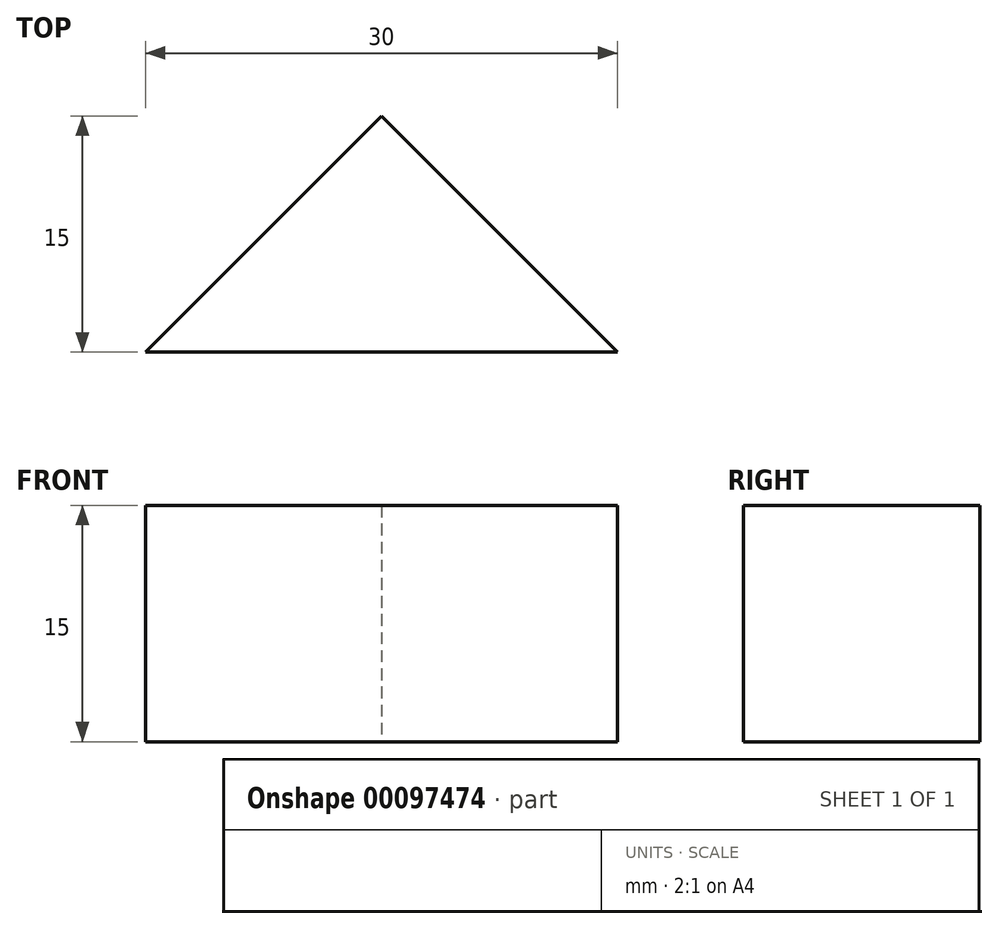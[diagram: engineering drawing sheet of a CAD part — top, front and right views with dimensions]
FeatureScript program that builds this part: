
annotation { "Feature Type Name" : "Feature", "Feature Type Description" : "" }
export const myFeature = defineFeature(function(context is Context, id is Id, definition is map)
    precondition{}
    {
        {
            var Q0;
            Q0=qCreatedBy(makeId("Top.planeOp"),FACE);
            var sketch = newSketch(context, id + "F0", { "sketchPlane" : qUnion([Q0])});
            skLineSegment(sketch, "E0", {"start": v(0, 0) * mm, "end": v(-30, 0) * mm});
            skLineSegment(sketch, "E1", {"start": v(-30, 0) * mm, "end": v(-15, 15) * mm});
            skPoint(sketch, "E1.endSnap0", {"position": v(-15, 0) * mm});
            skLineSegment(sketch, "E2", {"start": v(-15, 15) * mm, "end": v(0, 0) * mm});
            skSolve(sketch);
        }
        {
            var Q0;
            Q0=makeQuery(id+"F0.imprint","IMPRINT",FACE,{"disambiguationData":[TD([[makeQuery(id+"F0.imprint","IMPRINT",EDGE,{"derivedFrom":sQuery(id+"F0.wireOp",EDGE,"E0")}),-1.0]])]});
            extrude(context, id + "F1", {"entities" : qUnion([Q0]), "depth" : 15 * mm});
        }
    });
